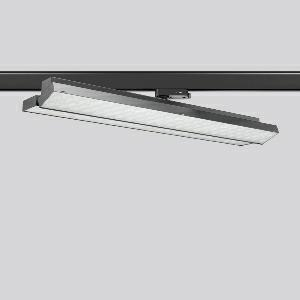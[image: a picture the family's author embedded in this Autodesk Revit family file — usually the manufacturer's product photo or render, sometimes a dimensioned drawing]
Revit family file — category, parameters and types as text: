
# Revit family: tx-move_742162_003_2_76_192c
name_source: partatom
category: Lighting Fixtures
units: mm (PartAtom-declared; Revit-internal decimal feet)

## family parameters
Cut with Voids When Loaded = No
Host = Face
Light Source = No
Part Type = Normal
Room Calculation Point = No
Round Connector Dimension = Use Diameter
Shared = No

## types (1)
- MultiLumen 1 (1 x LED Modul 927, 2100 lm, 2700)
    Apparent Load = 38 VA
    CIE Flux Codes = 77 96 99 100 100
    Color Rendering = 92
    Color Temperature = 2700
    Default Elevation = 1800 mm
    Description = Series: TX-MOVE
Multifunctional surface-mounted spotlight for area lighting. Very flat design. Housing: sheet steel, powder-coated. Rotation range: 356°. Swivel range: 90°. Consistent alignment possible with visible tilt scale. High-efficiency LED units with optimum light control thanks to clear plastic (PC) lens optics. Spezielle Mikrostrukturen reduzieren Gelbsaum. Symmetrical light distribution. Best colour rendering with CRI >90 for fresh products and coloured textiles. With adapter for RZB 3-circuit DALI tracks. Suitable for Track on ceiling. MultiLumen: Luminous flux adjustable in 3 steps. Factory setting is the highest luminous flux. Environmentally friendly and resource-saving due to replaceable and recyclable components. 
Colour: deep black, matt (RAL 9005)
Length: 570 mm
Width: 119 mm
Height: 88 mm
Lamp: LED
Socket: without socket
Colour temperature: 2700K
Colour rendering index (CRI): 90
System power: 38 W
Rated luminous flux: 4200 lm
Luminous efficiency: 111 lm/W
System power 2: 51 W
Rated luminous flux 2: 5500 lm
Luminous efficiency 2: 108 lm/W
System power 3: 62 W
Rated luminous flux 3: 6550 lm
Luminous efficiency 3: 106 lm/W
Control gear: Dimmable EVG, DALI
Protection class: I
Type of protection: IP 20
    Height = 75 mm
    Lamp = 1 x LED Modul 927
    Lamp Light Flux = 2100 lm
    Lamp count = 1
    Length = 569 mm
    Lifetime = 50000 h
    Luminous efficacy = 111 lm/W
    Manufacturer = RZB
    ModVariant = No
    Model = 742162.003.2.76
    Mounting Place = Ceiling
    Mounting Type = Surface mounted
    Number of Poles = 1
    OnlyDefault = Yes
    Power Factor = 1
    Product Name = TX-MOVE
    Product group = Track mounted projectors
    ProductGroupID = 301
    Protection Class = Protection class I
    Protection Degree = IP 20
    RLX_Detail_Level = 1
    RLX_Emergency_Light_Flux = 0 lm
    RLX_Emergency_Type = 0
    RLX_Emergency_Type_DB = No
    RlxData = <blob elided: 36957 chars, md5=101221b6>
    Socket = socket
    Standby Power = 0 W
    System Light Flux = 4200 lm
    System Power = 38 W
    Type Comments = MultiLumen 1
    Type Image = 742162.003.jpg
    URL = http://relux.com
    VarID = multilumen_1
    Voltage = 0 V
    Weight = 0.00 kg
    Width = 119 mm

## geometry (parser evidence)
native form markers: Blend x4, Sweep x14
no freeform markers — native parametric forms only
